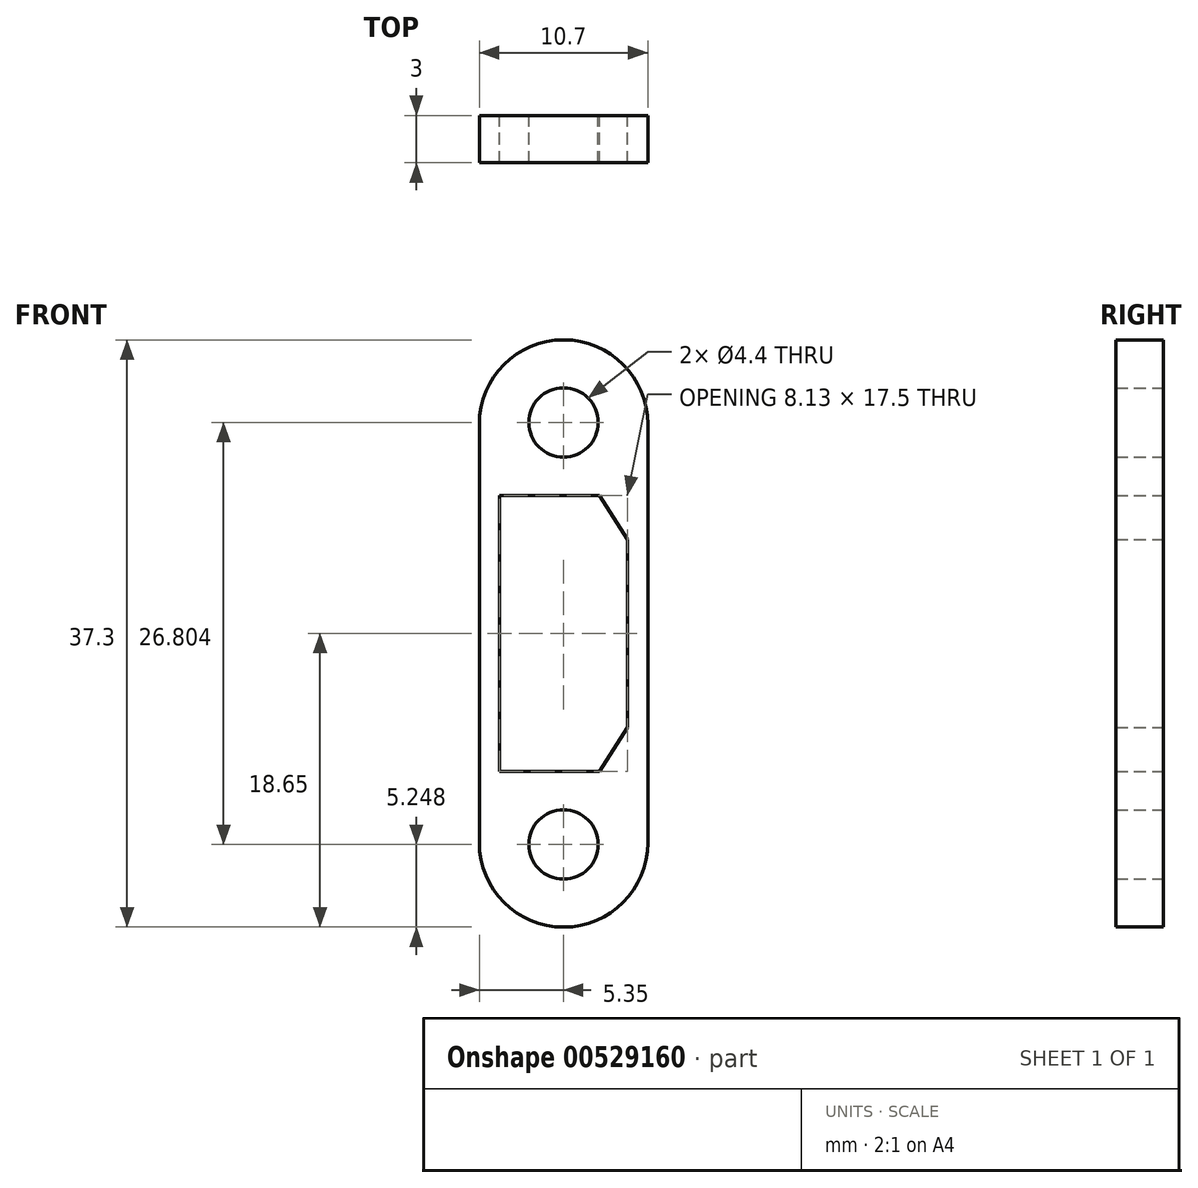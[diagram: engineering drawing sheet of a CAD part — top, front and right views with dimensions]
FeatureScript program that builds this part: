
annotation { "Feature Type Name" : "Feature", "Feature Type Description" : "" }
export const myFeature = defineFeature(function(context is Context, id is Id, definition is map)
    precondition{}
    {
        {
            var Q0;
            Q0=qCreatedBy(makeId("Front.planeOp"),FACE);
            var sketch = newSketch(context, id + "F0", { "sketchPlane" : qUnion([Q0])});
            skLineSegment(sketch, "E0.bottom", {"start": v(0.01, 18.65) * mm, "end": v(0, 18.65) * mm});
            skLineSegment(sketch, "E0.top", {"start": v(0.01, -18.65) * mm, "end": v(0, -18.65) * mm});
            skLineSegment(sketch, "E0.left", {"start": v(5.35, 13.3) * mm, "end": v(5.35, -13.3) * mm});
            skLineSegment(sketch, "E0.right", {"start": v(-5.35, 13.3) * mm, "end": v(-5.35, -13.3) * mm});
            skArc(sketch, "E1.filletArc", {"start": v(0, 18.65) * mm, "mid": v(-3.78, 17.08) * mm, "end": v(-5.35, 13.3) * mm});
            skArc(sketch, "E2.filletArc", {"start": v(-5.35, -13.3) * mm, "mid": v(-3.78, -17.08) * mm, "end": v(0, -18.65) * mm});
            skArc(sketch, "E3.filletArc", {"start": v(5.35, 13.3) * mm, "mid": v(3.79, 17.09) * mm, "end": v(0.01, 18.65) * mm});
            skArc(sketch, "E4.filletArc", {"start": v(0.01, -18.65) * mm, "mid": v(3.79, -17.09) * mm, "end": v(5.35, -13.3) * mm});
            skLineSegment(sketch, "E5", {"start": v(0, 18.65) * mm, "end": v(0.01, 18.65) * mm, "construction": true});
            skLineSegment(sketch, "E6", {"start": v(-12.29, 15.6) * mm, "end": v(11.5, 15.6) * mm, "construction": true});
            skLineSegment(sketch, "E7", {"start": v(-12.29, 13.4) * mm, "end": v(13.18, 13.4) * mm, "construction": true});
            skLineSegment(sketch, "E8", {"start": v(0, 19.95) * mm, "end": v(0, 8.14) * mm, "construction": true});
            skCircle(sketch, "E9", {"center": v(0, 13.4) * mm, "radius": 2.2 * mm});
            skCircle(sketch, "E10.MirrorC", {"center": v(0, -13.4) * mm, "radius": 2.2 * mm});
            skLineSegment(sketch, "E11.MirrorCS", {"start": v(-12.29, -13.4) * mm, "end": v(13.18, -13.4) * mm, "construction": true});
            skLineSegment(sketch, "E12.MirrorCS", {"start": v(-12.29, -15.6) * mm, "end": v(11.5, -15.6) * mm, "construction": true});
            skLineSegment(sketch, "E13.MirrorCS", {"start": v(0, -19.95) * mm, "end": v(0, -8.14) * mm, "construction": true});
            skLineSegment(sketch, "E14.bottom", {"start": v(2.29, -8.75) * mm, "end": v(-4.06, -8.75) * mm});
            skLineSegment(sketch, "E14.top", {"start": v(2.29, 8.75) * mm, "end": v(-4.06, 8.75) * mm});
            skLineSegment(sketch, "E14.left", {"start": v(4.06, -5.96) * mm, "end": v(4.06, 5.96) * mm});
            skLineSegment(sketch, "E14.right", {"start": v(-4.06, -8.75) * mm, "end": v(-4.06, 8.75) * mm});
            skPoint(sketch, "E14.middle", {"position": v(0, 0) * mm});
            skLineSegment(sketch, "E15", {"start": v(2.29, 10.1) * mm, "end": v(2.29, -10.2) * mm, "construction": true});
            skLineSegment(sketch, "E16", {"start": v(-6.3, 5.96) * mm, "end": v(7.6, 5.96) * mm, "construction": true});
            skLineSegment(sketch, "E17", {"start": v(2.29, 8.75) * mm, "end": v(4.06, 5.96) * mm});
            skLineSegment(sketch, "E18.MirrorCS", {"start": v(2.29, -8.75) * mm, "end": v(4.06, -5.96) * mm});
            skSolve(sketch);
        }
        {
            var Q0;
            Q0=makeQuery(id+"F0.imprint","IMPRINT",FACE,{"disambiguationData":[TD([[makeQuery(id+"F0.imprint","IMPRINT",EDGE,{"derivedFrom":sQuery(id+"F0.wireOp",EDGE,"E0.bottom")}),1.0]])]});
            extrude(context, id + "F1", {"entities" : qUnion([Q0]), "depth" : 3 * mm, "offsetDistance" : 25 * mm});
        }
    });
